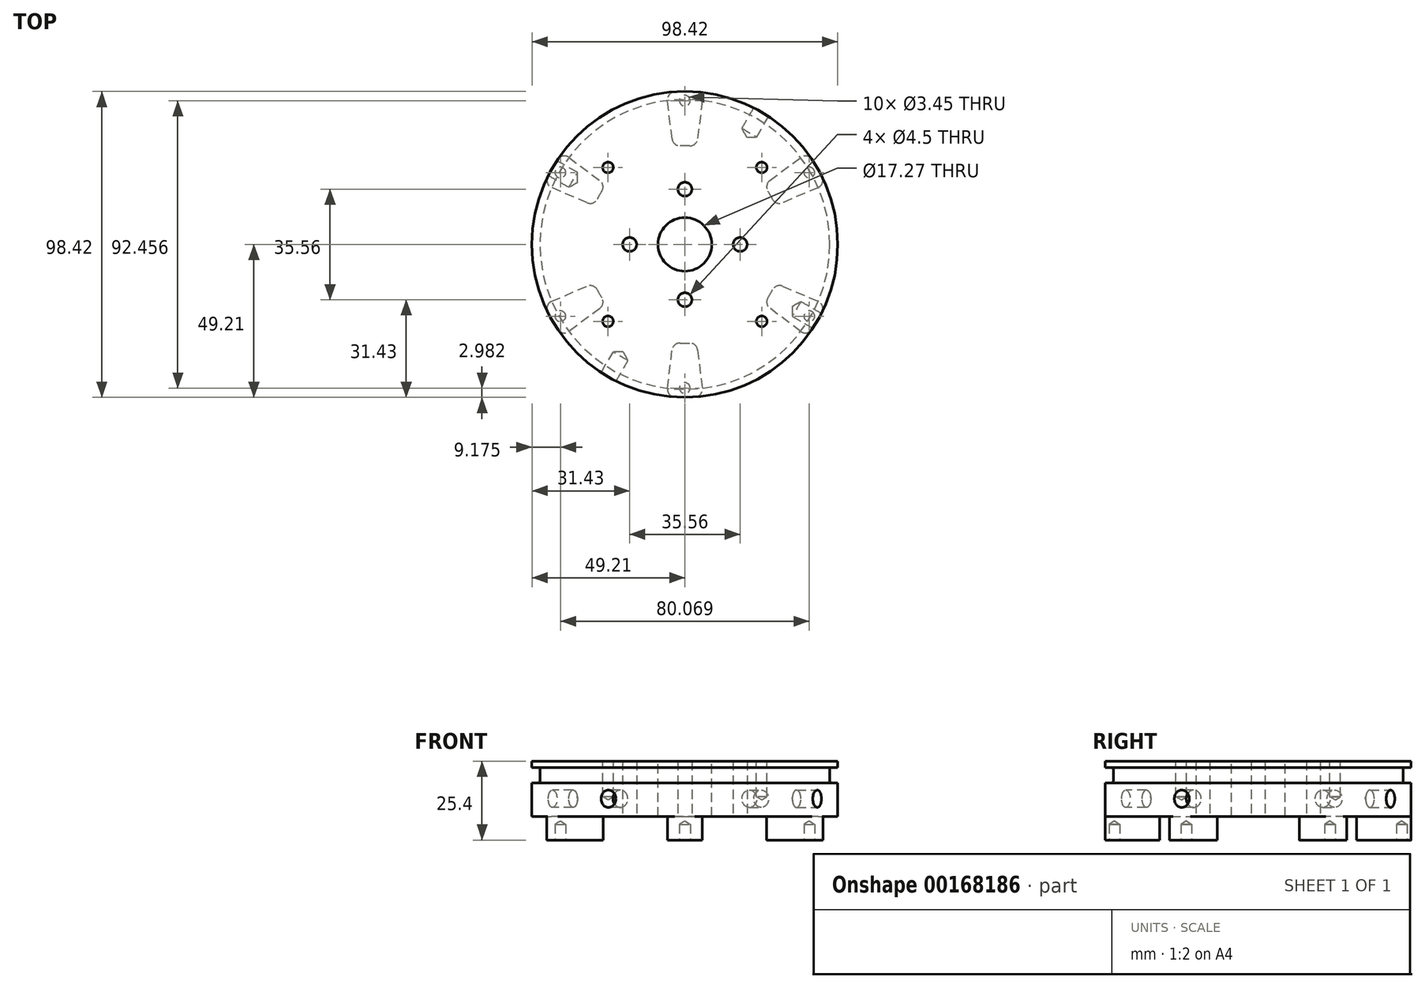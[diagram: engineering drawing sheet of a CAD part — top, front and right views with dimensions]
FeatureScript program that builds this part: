
annotation { "Feature Type Name" : "Feature", "Feature Type Description" : "" }
export const myFeature = defineFeature(function(context is Context, id is Id, definition is map)
    precondition{}
    {
        {
            var Q0;
            Q0=qCreatedBy(makeId("Top.planeOp"),FACE);
            var sketch = newSketch(context, id + "F0", { "sketchPlane" : qUnion([Q0])});
            skCircle(sketch, "E0", {"center": v(0, 0) * mm, "radius": 49.21 * mm});
            skSolve(sketch);
        }
        {
            var Q0;
            Q0=makeQuery(id+"F0.imprint","IMPRINT",FACE,{"disambiguationData":[TD([[makeQuery(id+"F0.imprint","IMPRINT",EDGE,{"derivedFrom":sQuery(id+"F0.wireOp",EDGE,"E0")}),1.0]])]});
            extrude(context, id + "F1", {"entities" : qUnion([Q0]), "depth" : 17.78 * mm});
        }
        {
            var Q0;
            Q0=makeQuery(id+"FNZgXB3MDCEPfWC_1.boolean.opBoolean","SPLIT",FACE,{"disambiguationData":[TD([makeQuery(id+"FNZgXB3MDCEPfWC_1.opExtrude","SWEPT_FACE",FACE,{"disambiguationData":[OSD([sQuery(id+"FiLk9hSRQ8Dv81E_1.wireOp",EDGE,"Xvq2NHEn-EDZK-GzOR-rNrk-moL4fFsD4KvI")])]})])],"derivedFrom":makeQuery(id+"F1.opExtrude","CAP_FACE",FACE,{"disambiguationData":[OSD([sQuery(id+"F0.wireOp",EDGE,"E0")])],"isStart":false})});
            var sketch = newSketch(context, id + "F2", { "sketchPlane" : qUnion([Q0])});
            skCircle(sketch, "E1", {"center": v(0, 0) * mm, "radius": 8.64 * mm});
            skSolve(sketch);
        }
        {
            var Q0;
            Q0=qSketchRegion(id+"F2",true);
            extrude(context, id + "F3", {"entities" : qUnion([Q0]), "operationType" : NewBodyOperationType.REMOVE, "endBound" : BoundingType.THROUGH_ALL, "oppositeDirection" : true, "depth" : 25.4 * mm});
        }
        {
            var Q0;
            Q0=makeQuery(id+"F1.opExtrude","CAP_FACE",FACE,{"disambiguationData":[OSD([sQuery(id+"F0.wireOp",EDGE,"E0")])],"isStart":true});
            var sketch = newSketch(context, id + "F4", { "sketchPlane" : qUnion([Q0])});
            skArc(sketch, "E2", {"start": v(-5.9, -48.86) * mm, "mid": v(0, -49.21) * mm, "end": v(5.9, -48.86) * mm});
            skArc(sketch, "E3", {"start": v(-3.81, -31.52) * mm, "mid": v(0, -31.75) * mm, "end": v(3.8, -31.52) * mm});
            skLineSegment(sketch, "E4", {"start": v(0, 0) * mm, "end": v(3.81, -31.52) * mm, "construction": true});
            skLineSegment(sketch, "E5", {"start": v(5.9, -48.86) * mm, "end": v(3.8, -31.52) * mm});
            skLineSegment(sketch, "E6", {"start": v(-3.8, -31.52) * mm, "end": v(-5.9, -48.86) * mm});
            skLineSegment(sketch, "E7", {"start": v(-3.81, -31.52) * mm, "end": v(3.81, -31.52) * mm, "construction": true});
            skPoint(sketch, "E8", {"position": v(0, -31.52) * mm});
            skLineSegment(sketch, "E9", {"start": v(0, 0) * mm, "end": v(-3.81, -31.52) * mm, "construction": true});
            skSolve(sketch);
        }
        {
            var Q0;
            Q0=qSketchRegion(id+"F4",true);
            extrude(context, id + "F5", {"entities" : qUnion([Q0]), "operationType" : NewBodyOperationType.ADD, "depth" : 7.62 * mm});
        }
        {
            var Q0;
            Q0=makeQuery(id+"F5.opExtrude","SWEPT_EDGE",EDGE,{"disambiguationData":[OSD([sQuery(id+"F0.wireOp",EDGE,"E0"),sQuery(id+"F4.wireOp",EDGE,"E2"),sQuery(id+"F4.wireOp",EDGE,"E5")])]});
            var Q1;
            Q1=makeQuery(id+"F5.opExtrude","SWEPT_EDGE",EDGE,{"disambiguationData":[OSD([sQuery(id+"F4.wireOp",EDGE,"E3"),sQuery(id+"F4.wireOp",EDGE,"E5")])]});
            var Q2;
            Q2=makeQuery(id+"F5.opExtrude","SWEPT_EDGE",EDGE,{"disambiguationData":[OSD([sQuery(id+"F0.wireOp",EDGE,"E0"),sQuery(id+"F4.wireOp",EDGE,"E2"),sQuery(id+"F4.wireOp",EDGE,"sxsrdx0H-xiQs-OsdF-6Z6r-2XBd8uqwUAgb")])]});
            var Q3;
            Q3=makeQuery(id+"F5.opExtrude","SWEPT_EDGE",EDGE,{"disambiguationData":[OSD([sQuery(id+"F4.wireOp",EDGE,"E3"),sQuery(id+"F4.wireOp",EDGE,"sxsrdx0H-xiQs-OsdF-6Z6r-2XBd8uqwUAgb")])]});
            fillet(context, id + "F6", {"entities" : qUnion([Q0, Q1, Q2, Q3]), "radius" : 2.54 * mm, "tangentPropagation" : true, "allowEdgeOverflow" : false});
        }
        {
            var Q0;
            Q0=makeQuery(id+"F5.opExtrude","CAP_FACE",FACE,{"disambiguationData":[OSD([sQuery(id+"F4.wireOp",EDGE,"E2"),sQuery(id+"F4.wireOp",EDGE,"E3"),sQuery(id+"F4.wireOp",EDGE,"E5"),sQuery(id+"F4.wireOp",EDGE,"sxsrdx0H-xiQs-OsdF-6Z6r-2XBd8uqwUAgb")])],"isStart":false});
            var sketch = newSketch(context, id + "F7", { "sketchPlane" : qUnion([Q0])});
            skLineSegment(sketch, "E10", {"start": v(0, 0) * mm, "end": v(0, 0) * mm});
            skLineSegment(sketch, "E11", {"start": v(0, 0) * mm, "end": v(0, -49.1) * mm, "construction": true});
            skPoint(sketch, "E12.3.0", {"position": v(0, -46.23) * mm});
            skPoint(sketch, "E12.center", {"position": v(0, 0) * mm});
            skPoint(sketch, "E13.1.0", {"position": v(40.03, -23.11) * mm});
            skPoint(sketch, "E13.2.0", {"position": v(40.03, 23.11) * mm});
            skPoint(sketch, "E14.0.3.0", {"position": v(0, 46.23) * mm});
            skPoint(sketch, "E14.0.4.0", {"position": v(-40.03, 23.11) * mm});
            skPoint(sketch, "E14.0.5.0", {"position": v(-40.03, -23.11) * mm});
            skSolve(sketch);
        }
        {
            var Q0;
            Q0=makeQuery(id+"F1.opExtrude","SWEPT_BODY",BODY,{"disambiguationData":[OSD([sQuery(id+"F0.wireOp",EDGE,"E0")])]});
            var Q1;
            Q1=makeQuery(id+"F3.boolean.opBoolean","COPY",FACE,{"derivedFrom":makeQuery(id+"F3.opExtrude","SWEPT_FACE",FACE,{"disambiguationData":[OSD([sQuery(id+"F2.wireOp",EDGE,"E1")])]})});
            circularPattern(context, id + "F8", {"operationType" : NewBodyOperationType.ADD, "entities" : qUnion([Q0]), "axis" : qUnion([Q1]), "angle" : 360 * degree, "instanceCount" : 6, "equalSpace" : true});
        }
        {
            var Q0;
            Q0=sQuery(id+"F7.wireOp",VERTEX,"E12.3.0");
            var Q1;
            Q1=sQuery(id+"F7.wireOp",VERTEX,"E13.1.0");
            var Q2;
            Q2=sQuery(id+"F7.wireOp",VERTEX,"E13.2.0");
            var Q3;
            Q3=sQuery(id+"F7.wireOp",VERTEX,"E14.0.3.0");
            var Q4;
            Q4=sQuery(id+"F7.wireOp",VERTEX,"E14.0.4.0");
            var Q5;
            Q5=sQuery(id+"F7.wireOp",VERTEX,"E14.0.5.0");
            var Q6;
            Q6=makeQuery(id+"F1.opExtrude","SWEPT_BODY",BODY,{"disambiguationData":[OSD([sQuery(id+"F0.wireOp",EDGE,"E0")])]});
            hole(context, id + "F9", {"style" : HoleStyle.SIMPLE, "endStyle" : HoleEndStyle.BLIND, "standardTappedOrClearance" : lookupTablePath({ "standard" : "ANSI", "engagement" : "75%", "pitch" : "32 tpi", "size" : "#8", "type" : "Tapped" }), "standardBlindInLast" : lookupTablePath({ "standard" : "ANSI", "engagement" : "75%", "pitch" : "32 tpi", "size" : "#8", "type" : "Tapped" }), "holeDiameter" : 3.45 * mm, "holeDepth" : 5.08 * mm, "locations" : qUnion([Q0, Q1, Q2, Q3, Q4, Q5]), "scope" : qUnion([Q6]), "majorDiameter" : 4.17 * mm});
        }
        {
            var Q0;
            {var subQ0=makeQuery(id+"F3.boolean.opBoolean","COPY",FACE,{"derivedFrom":makeQuery(id+"F3.opExtrude","SWEPT_FACE",FACE,{"disambiguationData":[OSD([sQuery(id+"F2.wireOp",EDGE,"E1")])]})});Q0=makeQuery(id+"FOQC5dfjhO448EJ_1.boolean.opBoolean","SPLIT",FACE,{"disambiguationData":[TD([subQ0])],"derivedFrom":makeQuery(id+"FkcieFRIapZdHPD_1.boolean.opBoolean","SPLIT",FACE,{"disambiguationData":[TD([subQ0])],"derivedFrom":makeQuery(id+"F1.opExtrude","CAP_FACE",FACE,{"disambiguationData":[OSD([sQuery(id+"F0.wireOp",EDGE,"E0")])],"isStart":false})})});}
            var sketch = newSketch(context, id + "F10", { "sketchPlane" : qUnion([Q0])});
            skCircle(sketch, "E15", {"center": v(0, 0) * mm, "radius": 35 * mm, "construction": true});
            skLineSegment(sketch, "E16", {"start": v(0, 0) * mm, "end": v(35, 0) * mm, "construction": true});
            skPoint(sketch, "E17", {"position": v(35, 0) * mm});
            skLineSegment(sketch, "E18", {"start": v(0, 0) * mm, "end": v(24.75, -24.75) * mm, "construction": true});
            skPoint(sketch, "E19", {"position": v(24.75, -24.75) * mm});
            skPoint(sketch, "E20.1.0", {"position": v(24.75, 24.75) * mm});
            skPoint(sketch, "E20.2.0", {"position": v(-24.75, 24.75) * mm});
            skPoint(sketch, "E20.3.0", {"position": v(-24.75, -24.75) * mm});
            skSolve(sketch);
        }
        {
            var Q0;
            Q0=sQuery(id+"F10.wireOp",VERTEX,"E19");
            var Q1;
            Q1=sQuery(id+"F10.wireOp",VERTEX,"E20.3.0");
            var Q2;
            Q2=sQuery(id+"F10.wireOp",VERTEX,"E20.2.0");
            var Q3;
            Q3=sQuery(id+"F10.wireOp",VERTEX,"E20.1.0");
            var Q4;
            Q4=makeQuery(id+"F1.opExtrude","SWEPT_BODY",BODY,{"disambiguationData":[OSD([sQuery(id+"F0.wireOp",EDGE,"E0")])]});
            hole(context, id + "F11", {"style" : HoleStyle.SIMPLE, "endStyle" : HoleEndStyle.BLIND, "standardTappedOrClearance" : lookupTablePath({ "standard" : "ANSI", "engagement" : "75%", "pitch" : "32 tpi", "size" : "#8", "type" : "Tapped" }), "standardBlindInLast" : lookupTablePath({ "standard" : "ANSI", "engagement" : "75%", "pitch" : "32 tpi", "size" : "#8", "type" : "Tapped" }), "holeDiameter" : 3.45 * mm, "holeDepth" : 11.43 * mm, "locations" : qUnion([Q0, Q1, Q2, Q3]), "scope" : qUnion([Q4]), "majorDiameter" : 4.17 * mm});
        }
        {
            var Q0;
            Q0=makeQuery(id+"FOQC5dfjhO448EJ_1.boolean.opBoolean","SPLIT",FACE,{"disambiguationData":[TD([makeQuery(id+"F3.boolean.opBoolean","COPY",FACE,{"derivedFrom":makeQuery(id+"F3.opExtrude","SWEPT_FACE",FACE,{"disambiguationData":[OSD([sQuery(id+"F2.wireOp",EDGE,"E1")])]})})])],"derivedFrom":makeQuery(id+"F1.opExtrude","CAP_FACE",FACE,{"disambiguationData":[OSD([sQuery(id+"F0.wireOp",EDGE,"E0")])],"isStart":false})});
            cPlane(context, id + "F12", {"entities" : qUnion([Q0]), "cplaneType" : CPlaneType.OFFSET, "offset" : 2.03 * mm, "oppositeDirection" : true, "width" : 152.4 * mm, "height" : 152.4 * mm});
        }
        {
            var Q0;
            Q0=qCreatedBy(id+"F12.planeOp",FACE);
            var sketch = newSketch(context, id + "F13", { "sketchPlane" : qUnion([Q0])});
            skCircle(sketch, "E21", {"center": v(0, 0) * mm, "radius": 46.62 * mm});
            skCircle(sketch, "E22.0", {"center": v(0, 0) * mm, "radius": 49.21 * mm});
            skSolve(sketch);
        }
        {
            var Q0;
            Q0=qSketchRegion(id+"F13",true);
            extrude(context, id + "F14", {"entities" : qUnion([Q0]), "operationType" : NewBodyOperationType.REMOVE, "oppositeDirection" : true, "depth" : 5 * mm});
        }
        {
            var Q0;
            Q0=makeQuery(id+"F14.boolean.opBoolean","COPY",EDGE,{"derivedFrom":makeQuery(id+"F14.opExtrude","CAP_EDGE",EDGE,{"disambiguationData":[OSD([sQuery(id+"F13.wireOp",EDGE,"E21")])],"isStart":false})});
            var Q1;
            Q1=makeQuery(id+"F14.boolean.opBoolean","COPY",EDGE,{"derivedFrom":makeQuery(id+"F14.opExtrude","CAP_EDGE",EDGE,{"disambiguationData":[OSD([sQuery(id+"F13.wireOp",EDGE,"E21")])],"isStart":true})});
            fillet(context, id + "F15", {"entities" : qUnion([Q0, Q1]), "radius" : 0.76 * mm, "tangentPropagation" : true, "allowEdgeOverflow" : false});
        }
        {
            var Q0;
            {var subQ1=sQuery(id+"F0.wireOp",EDGE,"E0");var subQ2=makeQuery(id+"F1.opExtrude","SWEPT_FACE",FACE,{"disambiguationData":[OSD([subQ1])]});Q0=makeQuery(id+"FkcieFRIapZdHPD_1.boolean.opBoolean","SPLIT",FACE,{"disambiguationData":[TD([subQ2])],"derivedFrom":makeQuery(id+"F1.opExtrude","CAP_FACE",FACE,{"disambiguationData":[OSD([subQ1])],"isStart":false})});}
            var sketch = newSketch(context, id + "F16", { "sketchPlane" : qUnion([Q0])});
            skCircle(sketch, "E23.0", {"center": v(0, 0) * mm, "radius": 49.21 * mm, "construction": true});
            skPoint(sketch, "E24", {"position": v(-24.6, -42.62) * mm});
            skLineSegment(sketch, "E25", {"start": v(0, -49.21) * mm, "end": v(0, 0) * mm, "construction": true});
            skLineSegment(sketch, "E26", {"start": v(0, 0) * mm, "end": v(-17.96, -31.1) * mm, "construction": true});
            skLineSegment(sketch, "E27", {"start": v(-17.96, -31.1) * mm, "end": v(-24.6, -42.62) * mm, "construction": true});
            skLineSegment(sketch, "E28", {"start": v(0, 0) * mm, "end": v(24.6, 42.62) * mm, "construction": true});
            skLineSegment(sketch, "E29", {"start": v(24.6, 42.62) * mm, "end": v(0, 0) * mm, "construction": true});
            skLineSegment(sketch, "E30", {"start": v(42.62, -24.6) * mm, "end": v(0, 0) * mm, "construction": true});
            skLineSegment(sketch, "E31", {"start": v(0, 0) * mm, "end": v(-42.62, 24.6) * mm, "construction": true});
            skPoint(sketch, "E32", {"position": v(24.6, 42.62) * mm});
            skPoint(sketch, "E33", {"position": v(42.62, -24.6) * mm});
            skPoint(sketch, "E34", {"position": v(-42.62, 24.6) * mm});
            skSolve(sketch);
        }
        {
            var Q0;
            Q0=qCreatedBy(makeId("Front.planeOp"),FACE);
            var sketch = newSketch(context, id + "F17", { "sketchPlane" : qUnion([Q0])});
            skLineSegment(sketch, "E35", {"start": v(0, 0) * mm, "end": v(0, 38.57) * mm, "construction": true});
            skSolve(sketch);
        }
        {
            var Q0;
            Q0=sQuery(id+"F17.wireOp",EDGE,"E35");
            cPlane(context, id + "F18", {"entities" : qUnion([Q0]), "cplaneType" : CPlaneType.LINE_ANGLE, "offset" : 25.4 * mm, "angle" : 60 * degree, "width" : 152.4 * mm, "height" : 152.4 * mm});
        }
        {
            var Q0;
            Q0=sQuery(id+"F16.wireOp",VERTEX,"E24");
            var Q1;
            Q1=qCreatedBy(id+"F18.planeOp",FACE);
            cPlane(context, id + "F19", {"entities" : qUnion([Q0, Q1]), "cplaneType" : CPlaneType.PLANE_POINT, "offset" : 25.4 * mm, "width" : 152.4 * mm, "height" : 152.4 * mm});
        }
        {
            var Q0;
            Q0=qCreatedBy(id+"F19.planeOp",FACE);
            var Q1;
            Q1=sQuery(id+"F16.wireOp",VERTEX,"E32");
            cPlane(context, id + "F20", {"entities" : qUnion([Q0, Q1]), "cplaneType" : CPlaneType.PLANE_POINT, "offset" : 25.4 * mm, "width" : 152.4 * mm, "height" : 152.4 * mm});
        }
        {
            var Q0;
            Q0=sQuery(id+"F17.wireOp",EDGE,"E35");
            cPlane(context, id + "F21", {"entities" : qUnion([Q0]), "cplaneType" : CPlaneType.LINE_ANGLE, "offset" : 25.4 * mm, "angle" : 150 * degree, "width" : 152.4 * mm, "height" : 152.4 * mm});
        }
        {
            var Q0;
            Q0=sQuery(id+"F16.wireOp",VERTEX,"E34");
            var Q1;
            Q1=qCreatedBy(id+"F21.planeOp",FACE);
            cPlane(context, id + "F22", {"entities" : qUnion([Q0, Q1]), "cplaneType" : CPlaneType.PLANE_POINT, "offset" : 25.4 * mm, "width" : 152.4 * mm, "height" : 152.4 * mm});
        }
        {
            var Q0;
            Q0=qCreatedBy(id+"F21.planeOp",FACE);
            var Q1;
            Q1=sQuery(id+"F16.wireOp",VERTEX,"E33");
            cPlane(context, id + "F23", {"entities" : qUnion([Q0, Q1]), "cplaneType" : CPlaneType.PLANE_POINT, "offset" : 25.4 * mm, "width" : 152.4 * mm, "height" : 152.4 * mm});
        }
        {
            var Q0;
            Q0=qCreatedBy(id+"F19.planeOp",FACE);
            var sketch = newSketch(context, id + "F24", { "sketchPlane" : qUnion([Q0])});
            skLineSegment(sketch, "E36", {"start": v(0, 0) * mm, "end": v(0, 5.66) * mm, "construction": true});
            skPoint(sketch, "E37", {"position": v(0, 5.66) * mm});
            skSolve(sketch);
        }
        {
            var Q0;
            Q0=qCreatedBy(id+"F20.planeOp",FACE);
            var sketch = newSketch(context, id + "F25", { "sketchPlane" : qUnion([Q0])});
            skPoint(sketch, "E38", {"position": v(0, 5.66) * mm});
            skLineSegment(sketch, "E39.0", {"start": v(0, 0) * mm, "end": v(0, 5.66) * mm, "construction": true});
            skSolve(sketch);
        }
        {
            var Q0;
            Q0=qCreatedBy(id+"F22.planeOp",FACE);
            var sketch = newSketch(context, id + "F26", { "sketchPlane" : qUnion([Q0])});
            skLineSegment(sketch, "E40", {"start": v(0, 0) * mm, "end": v(0, 5.66) * mm, "construction": true});
            skLineSegment(sketch, "E41.0", {"start": v(-49.21, 0) * mm, "end": v(-49.21, 5.66) * mm, "construction": true});
            skPoint(sketch, "E42", {"position": v(0, 5.66) * mm});
            skLineSegment(sketch, "E43", {"start": v(-49.21, 5.66) * mm, "end": v(0, 5.66) * mm, "construction": true});
            skSolve(sketch);
        }
        {
            var Q0;
            Q0=qCreatedBy(id+"F23.planeOp",FACE);
            var sketch = newSketch(context, id + "F27", { "sketchPlane" : qUnion([Q0])});
            skLineSegment(sketch, "E44.0", {"start": v(0, 0) * mm, "end": v(0, 5.66) * mm, "construction": true});
            skPoint(sketch, "E45", {"position": v(0, 5.66) * mm});
            skSolve(sketch);
        }
        {
            var Q0;
            Q0=sQuery(id+"F27.wireOp",VERTEX,"E45");
            var Q1;
            Q1=makeQuery(id+"F1.opExtrude","SWEPT_BODY",BODY,{"disambiguationData":[OSD([sQuery(id+"F0.wireOp",EDGE,"E0")])]});
            hole(context, id + "F28", {"style" : HoleStyle.SIMPLE, "endStyle" : HoleEndStyle.BLIND, "oppositeDirection" : true, "standardTappedOrClearance" : lookupTablePath({ "standard" : "ANSI", "engagement" : "75%", "pitch" : "32 tpi", "size" : "1/4", "type" : "Tapped" }), "standardBlindInLast" : lookupTablePath({ "standard" : "ANSI", "engagement" : "75%", "pitch" : "32 tpi", "size" : "1/4", "type" : "Tapped" }), "holeDiameter" : 5.56 * mm, "holeDepth" : 7.62 * mm, "locations" : qUnion([Q0]), "scope" : qUnion([Q1]), "majorDiameter" : 6.35 * mm});
        }
        {
            var Q0;
            Q0=sQuery(id+"F26.wireOp",VERTEX,"E42");
            var Q1;
            Q1=makeQuery(id+"F1.opExtrude","SWEPT_BODY",BODY,{"disambiguationData":[OSD([sQuery(id+"F0.wireOp",EDGE,"E0")])]});
            hole(context, id + "F29", {"style" : HoleStyle.SIMPLE, "endStyle" : HoleEndStyle.BLIND, "standardTappedOrClearance" : lookupTablePath({ "standard" : "ANSI", "engagement" : "75%", "pitch" : "32 tpi", "size" : "1/4", "type" : "Tapped" }), "standardBlindInLast" : lookupTablePath({ "standard" : "ANSI", "engagement" : "75%", "pitch" : "32 tpi", "size" : "1/4", "type" : "Tapped" }), "holeDiameter" : 5.56 * mm, "holeDepth" : 7.62 * mm, "locations" : qUnion([Q0]), "scope" : qUnion([Q1]), "majorDiameter" : 6.35 * mm});
        }
        {
            var Q0;
            Q0=sQuery(id+"F24.wireOp",VERTEX,"E37");
            var Q1;
            Q1=makeQuery(id+"F1.opExtrude","SWEPT_BODY",BODY,{"disambiguationData":[OSD([sQuery(id+"F0.wireOp",EDGE,"E0")])]});
            hole(context, id + "F30", {"style" : HoleStyle.SIMPLE, "endStyle" : HoleEndStyle.BLIND, "oppositeDirection" : true, "standardTappedOrClearance" : lookupTablePath({ "standard" : "ANSI", "engagement" : "75%", "pitch" : "32 tpi", "size" : "1/4", "type" : "Tapped" }), "standardBlindInLast" : lookupTablePath({ "standard" : "ANSI", "engagement" : "75%", "pitch" : "32 tpi", "size" : "1/4", "type" : "Tapped" }), "holeDiameter" : 5.56 * mm, "holeDepth" : 7.62 * mm, "locations" : qUnion([Q0]), "scope" : qUnion([Q1]), "majorDiameter" : 6.35 * mm});
        }
        {
            var Q0;
            Q0=sQuery(id+"F25.wireOp",VERTEX,"E38");
            var Q1;
            Q1=makeQuery(id+"F1.opExtrude","SWEPT_BODY",BODY,{"disambiguationData":[OSD([sQuery(id+"F0.wireOp",EDGE,"E0")])]});
            hole(context, id + "F31", {"style" : HoleStyle.SIMPLE, "endStyle" : HoleEndStyle.BLIND, "standardTappedOrClearance" : lookupTablePath({ "standard" : "ANSI", "engagement" : "75%", "pitch" : "32 tpi", "size" : "1/4", "type" : "Tapped" }), "standardBlindInLast" : lookupTablePath({ "standard" : "ANSI", "engagement" : "75%", "pitch" : "32 tpi", "size" : "1/4", "type" : "Tapped" }), "holeDiameter" : 5.56 * mm, "holeDepth" : 7.62 * mm, "locations" : qUnion([Q0]), "scope" : qUnion([Q1]), "majorDiameter" : 6.35 * mm});
        }
        {
            var Q0;
            Q0=makeQuery(id+"F1.opExtrude","CAP_FACE",FACE,{"disambiguationData":[OSD([sQuery(id+"F0.wireOp",EDGE,"E0")])],"isStart":true});
            var sketch = newSketch(context, id + "F32", { "sketchPlane" : qUnion([Q0])});
            skLineSegment(sketch, "E46", {"start": v(0, 0) * mm, "end": v(0, -17.78) * mm, "construction": true});
            skPoint(sketch, "E47", {"position": v(0, -17.78) * mm});
            skPoint(sketch, "E48.1.0", {"position": v(17.78, 0) * mm});
            skPoint(sketch, "E48.2.0", {"position": v(0, 17.78) * mm});
            skPoint(sketch, "E48.3.0", {"position": v(-17.78, 0) * mm});
            skPoint(sketch, "E48.center", {"position": v(0, 0) * mm});
            skSolve(sketch);
        }
        {
            var Q0;
            Q0=sQuery(id+"F32.wireOp",VERTEX,"E48.3.0");
            var Q1;
            Q1=sQuery(id+"F32.wireOp",VERTEX,"E47");
            var Q2;
            Q2=sQuery(id+"F32.wireOp",VERTEX,"E48.1.0");
            var Q3;
            Q3=sQuery(id+"F32.wireOp",VERTEX,"E48.2.0");
            var Q4;
            Q4=makeQuery(id+"F1.opExtrude","SWEPT_BODY",BODY,{"disambiguationData":[OSD([sQuery(id+"F0.wireOp",EDGE,"E0")])]});
            hole(context, id + "F33", {"style" : HoleStyle.SIMPLE, "endStyle" : HoleEndStyle.THROUGH, "standardTappedOrClearance" : lookupTablePath({ "standard" : "ANSI", "fit" : "Normal (ASME)", "size" : "#8", "type" : "Clearance" }), "standardBlindInLast" : lookupTablePath({ "fit" : "Free", "standard" : "ANSI", "size" : "#8", "type" : "Clearance" }), "holeDiameter" : 4.5 * mm, "locations" : qUnion([Q0, Q1, Q2, Q3]), "scope" : qUnion([Q4]), "isTappedThrough" : true});
        }
    });
